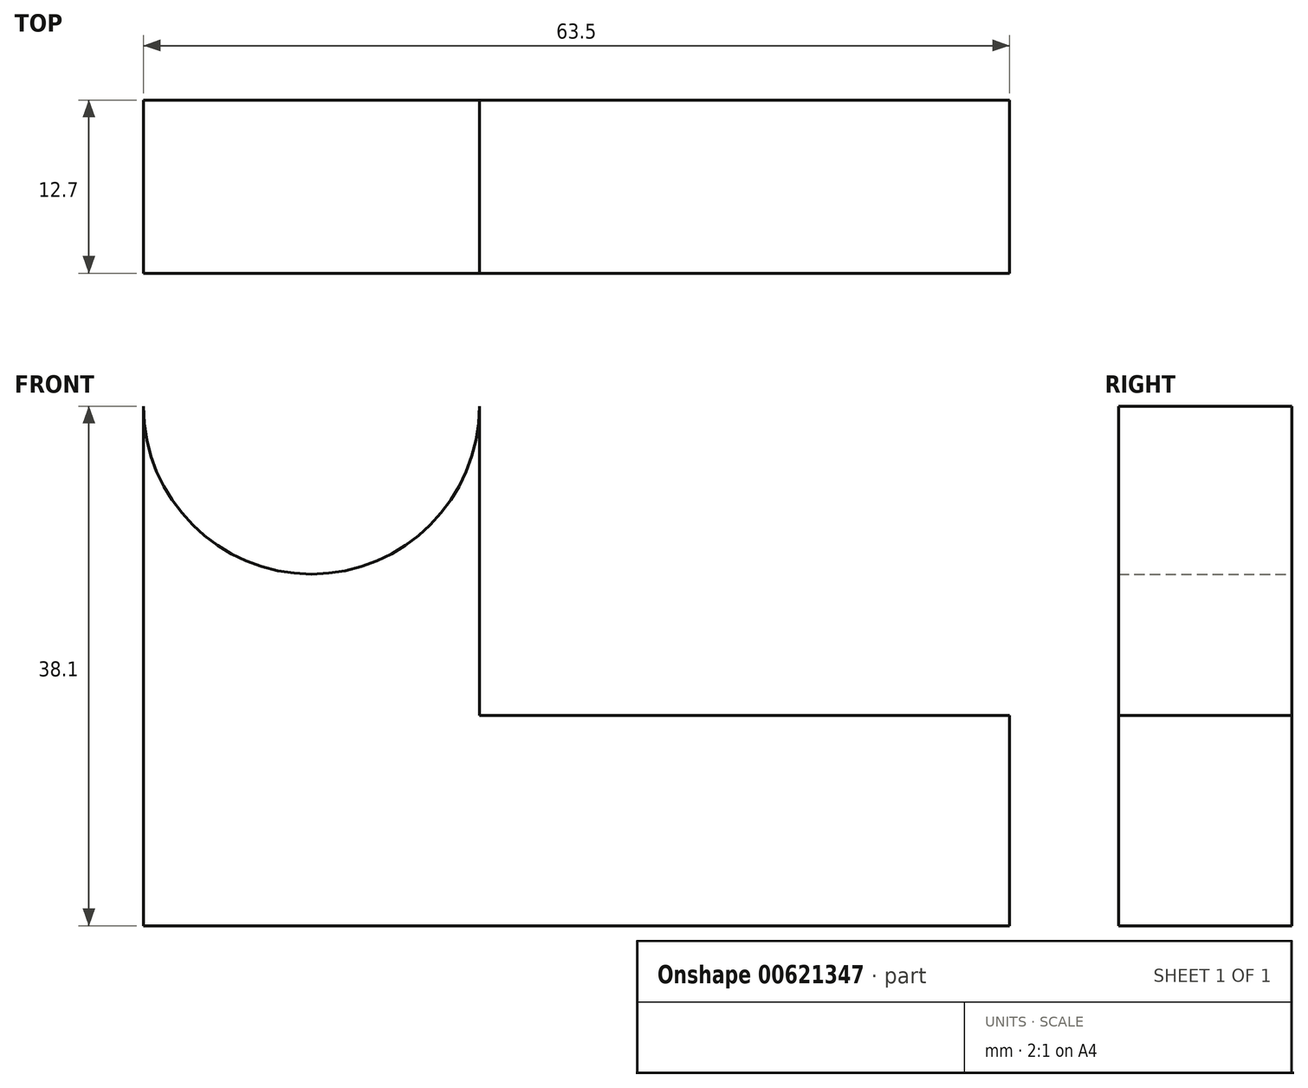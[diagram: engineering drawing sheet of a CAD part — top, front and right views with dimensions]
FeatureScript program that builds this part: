
annotation { "Feature Type Name" : "Feature", "Feature Type Description" : "" }
export const myFeature = defineFeature(function(context is Context, id is Id, definition is map)
    precondition{}
    {
        {
            var Q0;
            Q0=qCreatedBy(makeId("Front.planeOp"),FACE);
            var sketch = newSketch(context, id + "F0", { "sketchPlane" : qUnion([Q0])});
            skLineSegment(sketch, "E0", {"start": v(0, 38.1) * mm, "end": v(0, 0) * mm});
            skLineSegment(sketch, "E1", {"start": v(0, 0) * mm, "end": v(63.5, 0) * mm});
            skLineSegment(sketch, "E2", {"start": v(63.5, 0) * mm, "end": v(63.5, 15.42) * mm});
            skLineSegment(sketch, "E3", {"start": v(63.5, 15.42) * mm, "end": v(24.63, 15.42) * mm});
            skLineSegment(sketch, "E4", {"start": v(24.63, 15.42) * mm, "end": v(24.63, 38.1) * mm});
            skArc(sketch, "E5", {"start": v(0, 38.1) * mm, "mid": v(12.32, 25.78) * mm, "end": v(24.63, 38.1) * mm});
            skSolve(sketch);
        }
        {
            var Q0;
            Q0=makeQuery(id+"F0.imprint","IMPRINT",FACE,{"disambiguationData":[TD([[makeQuery(id+"F0.imprint","IMPRINT",EDGE,{"derivedFrom":sQuery(id+"F0.wireOp",EDGE,"E0")}),1.0]])]});
            extrude(context, id + "F1", {"entities" : qUnion([Q0]), "depth" : 12.7 * mm, "offsetDistance" : 25.4 * mm});
        }
    });
